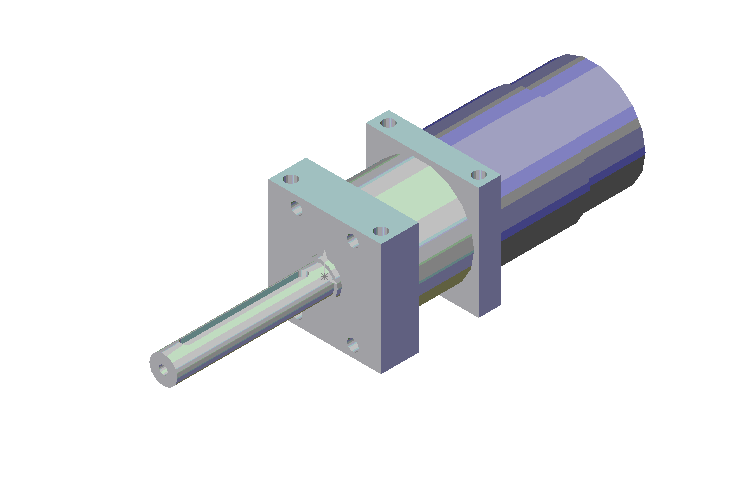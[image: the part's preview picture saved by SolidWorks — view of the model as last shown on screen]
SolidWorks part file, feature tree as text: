
SOLIDWORKS PART (.sldprt)
format: sldprt  version: not decoded by parser v0  size: 533,504 bytes
history: native  units: mm
features: sketch x14, extrude x7, cut_extrude x7, plane x2 (+8 scaffold rows collapsed)
feature tree (38):
  scaffold x8  (default folders/planes/origin — collapsed)
  sketch  "Sketch1"  dims[D13=4.0mm D14=4.0mm D15=4.0mm D16=4.0mm D1=19.05mm D2=38.1mm D3=19.05mm D4=38.1mm D5=9.525mm D6=9.53mm D7=9.53mm D8=9.53mm D9=3.81mm D10=3.81mm D11=34.29mm D12=34.29mm]
  extrude  "Base-Extrude"  Depth=12.7mm
  sketch  "Sketch2"  dims[D1=9.525mm]
  extrude  "Boss-Extrude1"  Depth=54.61mm
  plane  "Plane1"
  sketch  "Sketch3"  dims[D1=3.175mm D2=3.175mm D3=7.62mm D4=39.37mm]
  plane  "Plane2"  Offset=2.7625mm
  cut_extrude  "Cut-Extrude3"  [1 undecoded]
  sketch  "Sketch4"  dims[D1=3.0mm]
  cut_extrude  "Cut-Extrude4"  Depth=9.525mm
  sketch  "Sketch5"
  extrude  "Boss-Extrude2"  Depth=1.5mm
  sketch  "Sketch6"  dims[D1=4.0mm D2=4.0mm D3=3.81mm D4=34.29mm D5=3.81mm D6=3.81mm]
  cut_extrude  "Cut-Extrude5"  Depth=9.5mm
  sketch  "Sketch7"  dims[D1=15.24mm]
  cut_extrude  "Cut-Extrude6"  Depth=9.5mm
  sketch  "Sketch8"  dims[D1=35.0mm]
  extrude  "Boss-Extrude3"  Depth=20.32mm
  sketch  "Sketch9"
  extrude  "Boss-Extrude4"  Depth=7.62mm
  sketch  "Sketch11"  dims[c1.D7=4.0mm c1.D8=4.0mm c1.D9=4.0mm c1.D10=4.0mm c1.D11=4.0mm c1.D12=4.0mm c1.D13=4.0mm c1.D14=4.0mm c1.D1=9.525mm c1.D2=9.525mm c1.D3=28.575mm c1.D4=28.575mm c1.D5=3.81mm c1.D6=34.29mm c1.D15=9.53mm c1.D16=~31.774804mm c1.D17=28.58mm c1.D18=3.81mm c2.D16=34.29mm]
  cut_extrude  "Cut-Extrude7"  Depth=9.525mm
  sketch  "Sketch12"  dims[c1.D3=4.0mm c1.D4=4.0mm c1.D1=3.81mm c1.D2=3.81mm c2.D3=3.81mm c2.D5=3.81mm]
  cut_extrude  "Cut-Extrude8"  Depth=9.525mm
  sketch  "Sketch13"
  cut_extrude  "Cut-Extrude9"  Depth=9.525mm
  sketch  "Sketch14"  dims[D1=35.814mm]
  extrude  "Boss-Extrude5"  Depth=50mm
  sketch  "Sketch15"  dims[D1=38.1mm]
  extrude  "Boss-Extrude6"  Depth=30mm
decode coverage: 24 of 28 modeling features carry decoded parameters
note: ~ marks probable driven/reference dimensions
note: 1 parameter value undecoded
note: suppression state not decoded; provenance and decode notes live in map.json
